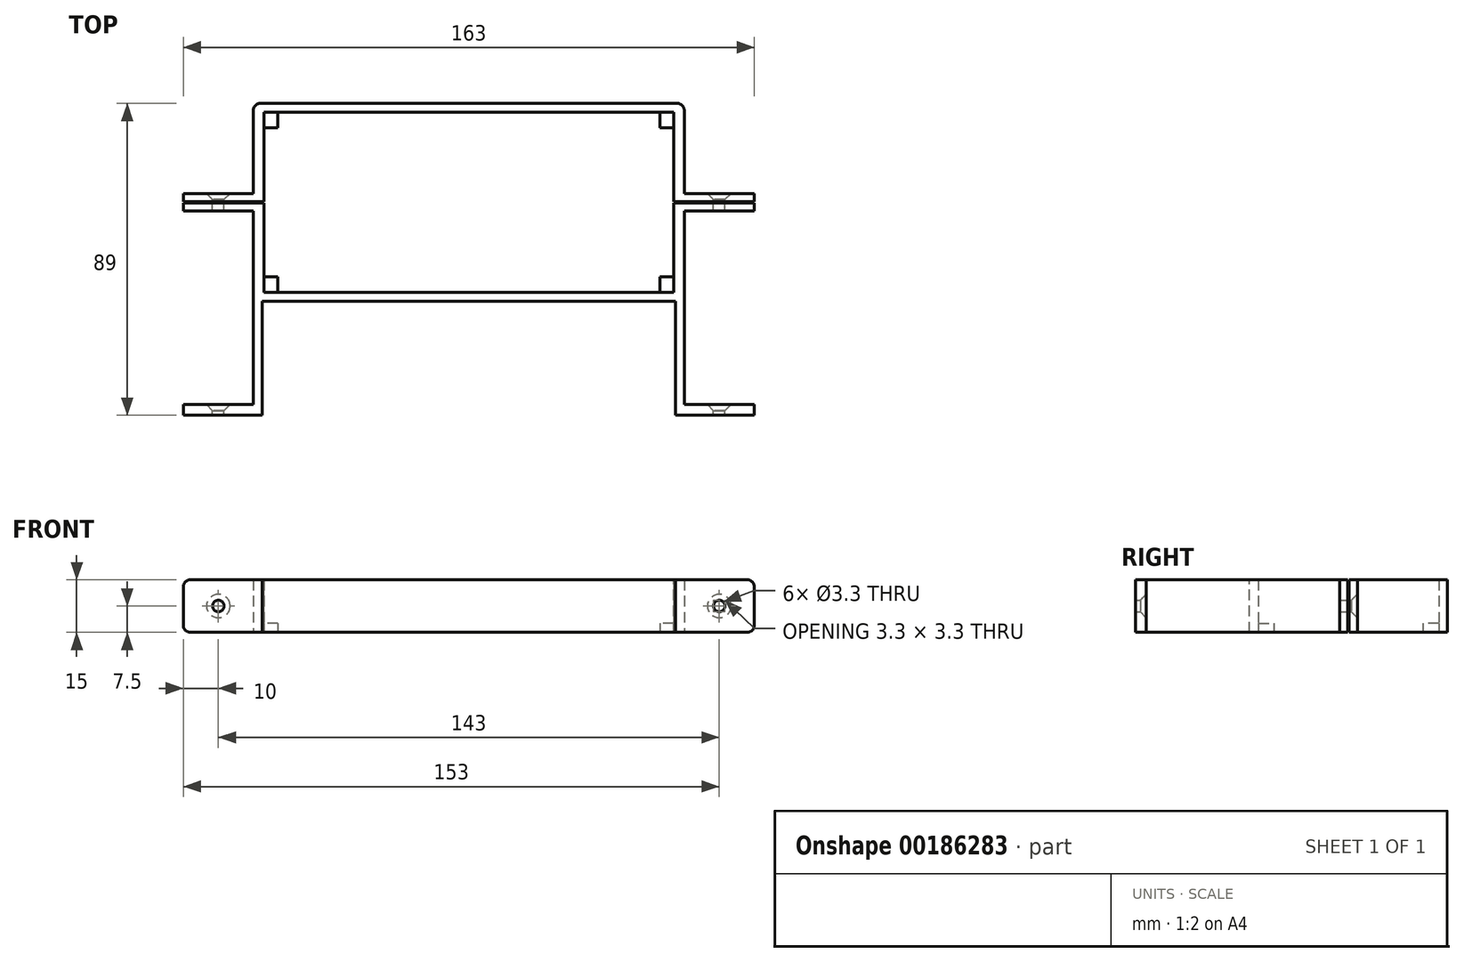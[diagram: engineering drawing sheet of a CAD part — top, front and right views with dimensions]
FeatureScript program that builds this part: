
annotation { "Feature Type Name" : "Feature", "Feature Type Description" : "" }
export const myFeature = defineFeature(function(context is Context, id is Id, definition is map)
    precondition{}
    {
        {
            var Q0;
            Q0=qCreatedBy(makeId("Top.planeOp"),FACE);
            var sketch = newSketch(context, id + "F0", { "sketchPlane" : qUnion([Q0])});
            skLineSegment(sketch, "E0.bottom", {"start": v(61.5, -28.25) * mm, "end": v(-61.5, -28.25) * mm});
            skLineSegment(sketch, "E0.top", {"start": v(61.5, 28.25) * mm, "end": v(-61.5, 28.25) * mm});
            skLineSegment(sketch, "E0.left", {"start": v(61.5, -28.25) * mm, "end": v(61.5, 28.25) * mm});
            skLineSegment(sketch, "E0.right", {"start": v(-61.5, -28.25) * mm, "end": v(-61.5, 28.25) * mm});
            skPoint(sketch, "E0.middle", {"position": v(0, 0) * mm});
            skLineSegment(sketch, "E1.bottom", {"start": v(58.5, -25.75) * mm, "end": v(-58.5, -25.75) * mm});
            skLineSegment(sketch, "E1.top", {"start": v(58.5, 25.75) * mm, "end": v(-58.5, 25.75) * mm});
            skLineSegment(sketch, "E1.left", {"start": v(58.5, -25.75) * mm, "end": v(58.5, 25.75) * mm});
            skLineSegment(sketch, "E1.right", {"start": v(-58.5, -25.75) * mm, "end": v(-58.5, 25.75) * mm});
            skSolve(sketch);
        }
        {
            var Q0;
            Q0=makeQuery(id+"F0.imprint","IMPRINT",FACE,{"disambiguationData":[TD([[makeQuery(id+"F0.imprint","IMPRINT",EDGE,{"derivedFrom":sQuery(id+"F0.wireOp",EDGE,"E0.bottom")}),-1.0]])]});
            extrude(context, id + "F1", {"entities" : qUnion([Q0]), "depth" : 15 * mm, "offsetDistance" : 25 * mm});
        }
        {
            var Q0;
            Q0=makeQuery(id+"F1.opExtrude","CAP_FACE",FACE,{"disambiguationData":[OSD([sQuery(id+"F0.wireOp",EDGE,"E0.bottom"),sQuery(id+"F0.wireOp",EDGE,"E0.top"),sQuery(id+"F0.wireOp",EDGE,"E0.left"),sQuery(id+"F0.wireOp",EDGE,"E0.right"),sQuery(id+"F0.wireOp",EDGE,"E1.bottom"),sQuery(id+"F0.wireOp",EDGE,"E1.top"),sQuery(id+"F0.wireOp",EDGE,"E1.left"),sQuery(id+"F0.wireOp",EDGE,"E1.right")])],"isStart":false});
            var sketch = newSketch(context, id + "F2", { "sketchPlane" : qUnion([Q0])});
            skLineSegment(sketch, "E2.bottom", {"start": v(-55, -25) * mm, "end": v(55, -25) * mm});
            skLineSegment(sketch, "E2.top", {"start": v(-55, 25) * mm, "end": v(55, 25) * mm});
            skLineSegment(sketch, "E2.left", {"start": v(-55, -25) * mm, "end": v(-55, 25) * mm});
            skLineSegment(sketch, "E2.right", {"start": v(55, -25) * mm, "end": v(55, 25) * mm});
            skPoint(sketch, "E2.middle", {"position": v(0, 0) * mm});
            skSolve(sketch);
        }
        {
            var Q0;
            Q0=makeQuery(id+"F1.opExtrude","SWEPT_FACE",FACE,{"disambiguationData":[OSD([sQuery(id+"F0.wireOp",EDGE,"E0.bottom")])]});
            var sketch = newSketch(context, id + "F3", { "sketchPlane" : qUnion([Q0])});
            skPoint(sketch, "E3", {"position": v(-59, 15) * mm});
            skPoint(sketch, "E4", {"position": v(-59, 0) * mm});
            skPoint(sketch, "E5", {"position": v(59, 15) * mm});
            skPoint(sketch, "E6", {"position": v(59, 0) * mm});
            skLineSegment(sketch, "E7", {"start": v(-59, 15) * mm, "end": v(-59, 0) * mm});
            skLineSegment(sketch, "E8", {"start": v(59, 0) * mm, "end": v(59, 15) * mm});
            skSolve(sketch);
        }
        {
            var Q0;
            {var subQ0=sQuery(id+"F3.wireOp",EDGE,"E7");Q0=makeQuery(id+"F3.imprint","IMPRINT",FACE,{"disambiguationData":[TD([[makeQuery(id+"F3.imprint","IMPRINT",EDGE,{"derivedFrom":subQ0}),-1.0]])]});}
            var Q1;
            {var subQ0=sQuery(id+"F3.wireOp",EDGE,"E8");Q1=makeQuery(id+"F3.imprint","IMPRINT",FACE,{"disambiguationData":[TD([[makeQuery(id+"F3.imprint","IMPRINT",EDGE,{"derivedFrom":subQ0}),-1.0]])]});}
            extrude(context, id + "F4", {"entities" : qUnion([Q0, Q1]), "operationType" : NewBodyOperationType.ADD, "depth" : 32.5 * mm, "offsetDistance" : 25 * mm});
        }
        {
            var Q0;
            {var subQ0=sQuery(id+"F0.wireOp",EDGE,"E0.right");Q0=makeQuery(id+"F4.boolean.opBoolean","MERGE",FACE,{"derivedFrom":[makeQuery(id+"F1.opExtrude","SWEPT_FACE",FACE,{"disambiguationData":[OSD([subQ0])]}),makeQuery(id+"F4.opExtrude","SWEPT_FACE",FACE,{"disambiguationData":[OSD([sQuery(id+"F0.wireOp",EDGE,"E0.bottom"),subQ0])]})]});}
            var sketch = newSketch(context, id + "F5", { "sketchPlane" : qUnion([Q0])});
            skPoint(sketch, "E9", {"position": v(57.75, 15) * mm});
            skPoint(sketch, "E10", {"position": v(57.75, 0) * mm});
            skLineSegment(sketch, "E11", {"start": v(57.75, 15) * mm, "end": v(57.75, 0) * mm});
            skSolve(sketch);
        }
        {
            var Q0;
            {var subQ0=sQuery(id+"F5.wireOp",EDGE,"E11");Q0=makeQuery(id+"F5.imprint","IMPRINT",FACE,{"disambiguationData":[TD([[makeQuery(id+"F5.imprint","IMPRINT",EDGE,{"derivedFrom":subQ0}),1.0]])]});}
            extrude(context, id + "F6", {"entities" : qUnion([Q0]), "operationType" : NewBodyOperationType.ADD, "depth" : 20 * mm, "offsetDistance" : 25 * mm});
        }
        {
            var Q0;
            {var subQ0=sQuery(id+"F0.wireOp",EDGE,"E0.left");Q0=makeQuery(id+"F4.boolean.opBoolean","MERGE",FACE,{"derivedFrom":[makeQuery(id+"F1.opExtrude","SWEPT_FACE",FACE,{"disambiguationData":[OSD([subQ0])]}),makeQuery(id+"F4.opExtrude","SWEPT_FACE",FACE,{"disambiguationData":[OSD([sQuery(id+"F0.wireOp",EDGE,"E0.bottom"),subQ0])]})]});}
            var sketch = newSketch(context, id + "F7", { "sketchPlane" : qUnion([Q0])});
            skPoint(sketch, "E12", {"position": v(-57.75, 15) * mm});
            skPoint(sketch, "E13", {"position": v(-57.75, 0) * mm});
            skLineSegment(sketch, "E14", {"start": v(-57.75, 15) * mm, "end": v(-57.75, 0) * mm});
            skSolve(sketch);
        }
        {
            var Q0;
            {var subQ0=sQuery(id+"F7.wireOp",EDGE,"E14");Q0=makeQuery(id+"F7.imprint","IMPRINT",FACE,{"disambiguationData":[TD([[makeQuery(id+"F7.imprint","IMPRINT",EDGE,{"derivedFrom":subQ0}),-1.0]])]});}
            extrude(context, id + "F8", {"entities" : qUnion([Q0]), "operationType" : NewBodyOperationType.ADD, "depth" : 20 * mm, "offsetDistance" : 25 * mm});
        }
        {
            var Q0;
            Q0=makeQuery(id+"F8.opExtrude","SWEPT_FACE",FACE,{"disambiguationData":[OSD([sQuery(id+"F7.wireOp",EDGE,"E14")])]});
            var sketch = newSketch(context, id + "F9", { "sketchPlane" : qUnion([Q0])});
            skPoint(sketch, "E15", {"position": v(-71.5, 7.5) * mm});
            skPoint(sketch, "E15.positionSnap0", {"position": v(-71.5, 0) * mm});
            skPoint(sketch, "E15.positionSnap1", {"position": v(-61.5, 7.5) * mm});
            skSolve(sketch);
        }
        {
            var Q0;
            Q0=sQuery(id+"F9.wireOp",VERTEX,"E15");
            var Q1;
            Q1=makeQuery(id+"F1.opExtrude","SWEPT_BODY",BODY,{"disambiguationData":[OSD([sQuery(id+"F0.wireOp",EDGE,"E0.bottom"),sQuery(id+"F0.wireOp",EDGE,"E0.top"),sQuery(id+"F0.wireOp",EDGE,"E0.left"),sQuery(id+"F0.wireOp",EDGE,"E0.right"),sQuery(id+"F0.wireOp",EDGE,"E1.bottom"),sQuery(id+"F0.wireOp",EDGE,"E1.top"),sQuery(id+"F0.wireOp",EDGE,"E1.left"),sQuery(id+"F0.wireOp",EDGE,"E1.right")])]});
            hole(context, id + "F10", {"style" : HoleStyle.C_SINK, "endStyle" : HoleEndStyle.BLIND, "standardTappedOrClearance" : lookupTablePath({ "standard" : "ISO", "fit" : "Normal", "size" : "M3", "type" : "Clearance" }), "standardBlindInLast" : lookupTablePath({ "fit" : "Standard", "standard" : "ISO", "size" : "M3", "type" : "Clearance" }), "holeDiameter" : 3.3 * mm, "cSinkDiameter" : 6.72 * mm, "cSinkAngle" : 90 * degree, "majorDiameter" : 5 * mm, "holeDepth" : 5 * mm, "isTappedThrough" : true, "tappedDepth" : 12 * mm, "tapClearance" : 3, "startFromSketch" : true, "locations" : qUnion([Q0]), "scope" : qUnion([Q1])});
        }
        {
            var Q0;
            Q0=makeQuery(id+"F6.opExtrude","SWEPT_FACE",FACE,{"disambiguationData":[OSD([sQuery(id+"F5.wireOp",EDGE,"E11")])]});
            var sketch = newSketch(context, id + "F11", { "sketchPlane" : qUnion([Q0])});
            skPoint(sketch, "E16", {"position": v(71.5, 7.5) * mm});
            skPoint(sketch, "E16.positionSnap0", {"position": v(81.5, 7.5) * mm});
            skPoint(sketch, "E16.positionSnap1", {"position": v(71.5, 0) * mm});
            skSolve(sketch);
        }
        {
            var Q0;
            Q0=sQuery(id+"F11.wireOp",VERTEX,"E16");
            var Q1;
            Q1=makeQuery(id+"F1.opExtrude","SWEPT_BODY",BODY,{"disambiguationData":[OSD([sQuery(id+"F0.wireOp",EDGE,"E0.bottom"),sQuery(id+"F0.wireOp",EDGE,"E0.top"),sQuery(id+"F0.wireOp",EDGE,"E0.left"),sQuery(id+"F0.wireOp",EDGE,"E0.right"),sQuery(id+"F0.wireOp",EDGE,"E1.bottom"),sQuery(id+"F0.wireOp",EDGE,"E1.top"),sQuery(id+"F0.wireOp",EDGE,"E1.left"),sQuery(id+"F0.wireOp",EDGE,"E1.right")])]});
            hole(context, id + "F12", {"style" : HoleStyle.C_SINK, "endStyle" : HoleEndStyle.BLIND, "standardTappedOrClearance" : lookupTablePath({ "standard" : "ISO", "fit" : "Normal", "size" : "M3", "type" : "Clearance" }), "standardBlindInLast" : lookupTablePath({ "fit" : "Standard", "standard" : "ISO", "size" : "M3", "type" : "Clearance" }), "holeDiameter" : 3.3 * mm, "cSinkDiameter" : 6.72 * mm, "cSinkAngle" : 90 * degree, "majorDiameter" : 5 * mm, "holeDepth" : 5 * mm, "isTappedThrough" : true, "tappedDepth" : 12 * mm, "tapClearance" : 3, "startFromSketch" : true, "locations" : qUnion([Q0]), "scope" : qUnion([Q1])});
        }
        {
            var Q0;
            {var subQ0=sQuery(id+"F0.wireOp",EDGE,"E0.bottom");var subQ1=makeQuery(id+"F1.opExtrude","CAP_EDGE",EDGE,{"disambiguationData":[OSD([subQ0])],"isStart":true});var subQ2=sQuery(id+"F0.wireOp",EDGE,"E0.left");var subQ3=makeQuery(id+"F3.imprint","INTERSECT",VERTEX,{"derivedFrom":[makeQuery(id+"F1.opExtrude","SWEPT_EDGE",EDGE,{"disambiguationData":[OSD([subQ0,subQ2])]}),subQ1]});var subQ4=makeQuery(id+"F4.boolean.opBoolean","MERGE",EDGE,{"derivedFrom":[makeQuery(id+"F1.opExtrude","CAP_EDGE",EDGE,{"disambiguationData":[OSD([subQ2])],"isStart":true}),makeQuery(id+"F4.opExtrude","SWEPT_EDGE",EDGE,{"disambiguationData":[OSD([subQ0,subQ2]),TDD([subQ3])]})]});var subQ5=sQuery(id+"F0.wireOp",EDGE,"E0.right");var subQ6=makeQuery(id+"F3.imprint","INTERSECT",VERTEX,{"derivedFrom":[makeQuery(id+"F1.opExtrude","SWEPT_EDGE",EDGE,{"disambiguationData":[OSD([subQ0,subQ5])]}),subQ1]});var subQ7=makeQuery(id+"F4.boolean.opBoolean","MERGE",EDGE,{"derivedFrom":[makeQuery(id+"F1.opExtrude","CAP_EDGE",EDGE,{"disambiguationData":[OSD([subQ5])],"isStart":true}),makeQuery(id+"F4.opExtrude","SWEPT_EDGE",EDGE,{"disambiguationData":[OSD([subQ0,subQ5]),TDD([subQ6])]})]});Q0=makeQuery(id+"F8.boolean.opBoolean","MERGE",FACE,{"derivedFrom":[makeQuery(id+"F6.boolean.opBoolean","MERGE",FACE,{"derivedFrom":[makeQuery(id+"F4.boolean.opBoolean","MERGE",FACE,{"derivedFrom":[makeQuery(id+"F1.opExtrude","CAP_FACE",FACE,{"disambiguationData":[OSD([subQ0,sQuery(id+"F0.wireOp",EDGE,"E0.top"),subQ2,subQ5,sQuery(id+"F0.wireOp",EDGE,"E1.bottom"),sQuery(id+"F0.wireOp",EDGE,"E1.top"),sQuery(id+"F0.wireOp",EDGE,"E1.left"),sQuery(id+"F0.wireOp",EDGE,"E1.right")])],"isStart":true}),makeQuery(id+"F4.opExtrude","SWEPT_FACE",FACE,{"disambiguationData":[OSD([subQ0]),TDD([makeQuery(id+"F3.imprint","IMPRINT",EDGE,{"disambiguationData":[TD([[makeQuery(id+"F3.imprint","INTERSECT",VERTEX,{"derivedFrom":[subQ1,sQuery(id+"F3.wireOp",EDGE,"E8")]}),1.0]])],"derivedFrom":subQ1})])]}),makeQuery(id+"F4.opExtrude","SWEPT_FACE",FACE,{"disambiguationData":[OSD([subQ0]),TDD([makeQuery(id+"F3.imprint","IMPRINT",EDGE,{"disambiguationData":[TD([[makeQuery(id+"F3.imprint","INTERSECT",VERTEX,{"derivedFrom":[subQ1,sQuery(id+"F3.wireOp",EDGE,"E7")]}),-1.0]])],"derivedFrom":subQ1})])]})]}),makeQuery(id+"F6.opExtrude","SWEPT_FACE",FACE,{"disambiguationData":[OSD([subQ0,subQ5]),TDD([makeQuery(id+"F5.imprint","IMPRINT",EDGE,{"disambiguationData":[TD([[makeQuery(id+"F5.imprint","INTERSECT",VERTEX,{"derivedFrom":[subQ7,sQuery(id+"F5.wireOp",EDGE,"E11")]}),1.0]])],"derivedFrom":subQ7})])]})]}),makeQuery(id+"F8.opExtrude","SWEPT_FACE",FACE,{"disambiguationData":[OSD([subQ0,subQ2]),TDD([makeQuery(id+"F7.imprint","IMPRINT",EDGE,{"disambiguationData":[TD([[makeQuery(id+"F7.imprint","INTERSECT",VERTEX,{"derivedFrom":[subQ4,sQuery(id+"F7.wireOp",EDGE,"E14")]}),1.0]])],"derivedFrom":subQ4})])]})]});}
            var sketch = newSketch(context, id + "F13", { "sketchPlane" : qUnion([Q0])});
            skPoint(sketch, "E17", {"position": v(59.5, -26.25) * mm});
            skPoint(sketch, "E18", {"position": v(-59.5, -26.25) * mm});
            skPoint(sketch, "E19", {"position": v(-59.5, 26.25) * mm});
            skPoint(sketch, "E20", {"position": v(59.5, 26.25) * mm});
            skLineSegment(sketch, "E21.bottom", {"start": v(59.5, -26.25) * mm, "end": v(54.5, -26.25) * mm});
            skLineSegment(sketch, "E21.top", {"start": v(59.5, -21.25) * mm, "end": v(54.5, -21.25) * mm});
            skLineSegment(sketch, "E21.left", {"start": v(59.5, -26.25) * mm, "end": v(59.5, -21.25) * mm});
            skLineSegment(sketch, "E21.right", {"start": v(54.5, -26.25) * mm, "end": v(54.5, -21.25) * mm});
            skLineSegment(sketch, "E22.bottom", {"start": v(-59.5, -26.25) * mm, "end": v(-54.5, -26.25) * mm});
            skLineSegment(sketch, "E22.top", {"start": v(-59.5, -21.25) * mm, "end": v(-54.5, -21.25) * mm});
            skLineSegment(sketch, "E22.left", {"start": v(-59.5, -26.25) * mm, "end": v(-59.5, -21.25) * mm});
            skLineSegment(sketch, "E22.right", {"start": v(-54.5, -26.25) * mm, "end": v(-54.5, -21.25) * mm});
            skLineSegment(sketch, "E23.bottom", {"start": v(-59.5, 26.25) * mm, "end": v(-54.5, 26.25) * mm});
            skLineSegment(sketch, "E23.top", {"start": v(-59.5, 21.25) * mm, "end": v(-54.5, 21.25) * mm});
            skLineSegment(sketch, "E23.left", {"start": v(-59.5, 26.25) * mm, "end": v(-59.5, 21.25) * mm});
            skLineSegment(sketch, "E23.right", {"start": v(-54.5, 26.25) * mm, "end": v(-54.5, 21.25) * mm});
            skLineSegment(sketch, "E24.bottom", {"start": v(59.5, 26.25) * mm, "end": v(54.5, 26.25) * mm});
            skLineSegment(sketch, "E24.top", {"start": v(59.5, 21.25) * mm, "end": v(54.5, 21.25) * mm});
            skLineSegment(sketch, "E24.left", {"start": v(59.5, 26.25) * mm, "end": v(59.5, 21.25) * mm});
            skLineSegment(sketch, "E24.right", {"start": v(54.5, 26.25) * mm, "end": v(54.5, 21.25) * mm});
            skSolve(sketch);
        }
        {
            var Q0;
            {var subQ0=sQuery(id+"F13.wireOp",EDGE,"E22.right");var subQ1=sQuery(id+"F13.wireOp",EDGE,"E22.top");var subQ2=makeQuery(id+"F13.imprint","INTERSECT",VERTEX,{"derivedFrom":[subQ1,subQ0]});Q0=makeQuery(id+"F13.imprint","IMPRINT",FACE,{"disambiguationData":[TD([[makeQuery(id+"F13.imprint","IMPRINT",EDGE,{"disambiguationData":[TD([[subQ2,1.0]])],"derivedFrom":subQ1}),-1.0]])]});}
            var Q1;
            {var subQ0=sQuery(id+"F13.wireOp",EDGE,"E23.right");var subQ1=sQuery(id+"F13.wireOp",EDGE,"E23.top");var subQ2=makeQuery(id+"F13.imprint","INTERSECT",VERTEX,{"derivedFrom":[subQ1,subQ0]});Q1=makeQuery(id+"F13.imprint","IMPRINT",FACE,{"disambiguationData":[TD([[makeQuery(id+"F13.imprint","IMPRINT",EDGE,{"disambiguationData":[TD([[subQ2,1.0]])],"derivedFrom":subQ1}),1.0]])]});}
            var Q2;
            {var subQ0=sQuery(id+"F13.wireOp",EDGE,"E24.right");var subQ1=sQuery(id+"F13.wireOp",EDGE,"E24.top");var subQ2=makeQuery(id+"F13.imprint","INTERSECT",VERTEX,{"derivedFrom":[subQ1,subQ0]});Q2=makeQuery(id+"F13.imprint","IMPRINT",FACE,{"disambiguationData":[TD([[makeQuery(id+"F13.imprint","IMPRINT",EDGE,{"disambiguationData":[TD([[subQ2,1.0]])],"derivedFrom":subQ1}),-1.0]])]});}
            var Q3;
            {var subQ0=sQuery(id+"F13.wireOp",EDGE,"E21.right");var subQ1=sQuery(id+"F13.wireOp",EDGE,"E21.top");var subQ2=makeQuery(id+"F13.imprint","INTERSECT",VERTEX,{"derivedFrom":[subQ1,subQ0]});Q3=makeQuery(id+"F13.imprint","IMPRINT",FACE,{"disambiguationData":[TD([[makeQuery(id+"F13.imprint","IMPRINT",EDGE,{"disambiguationData":[TD([[subQ2,1.0]])],"derivedFrom":subQ1}),1.0]])]});}
            extrude(context, id + "F14", {"entities" : qUnion([Q0, Q1, Q2, Q3]), "operationType" : NewBodyOperationType.ADD, "oppositeDirection" : true, "depth" : 2.5 * mm, "offsetDistance" : 25 * mm});
        }
        {
            var Q0;
            {var subQ0=sQuery(id+"F0.wireOp",EDGE,"E0.right");Q0=makeQuery(id+"F4.boolean.opBoolean","MERGE",FACE,{"derivedFrom":[makeQuery(id+"F1.opExtrude","SWEPT_FACE",FACE,{"disambiguationData":[OSD([subQ0])]}),makeQuery(id+"F4.opExtrude","SWEPT_FACE",FACE,{"disambiguationData":[OSD([sQuery(id+"F0.wireOp",EDGE,"E0.bottom"),subQ0])]})]});}
            var sketch = newSketch(context, id + "F15", { "sketchPlane" : qUnion([Q0])});
            skPoint(sketch, "E25", {"position": v(-2.5, 0) * mm});
            skPoint(sketch, "E26", {"position": v(2.5, 0) * mm});
            skPoint(sketch, "E27", {"position": v(2.5, 15) * mm});
            skPoint(sketch, "E28", {"position": v(-2.5, 15) * mm});
            skPoint(sketch, "E29", {"position": v(0, 0) * mm});
            skPoint(sketch, "E30", {"position": v(0, 15) * mm});
            skLineSegment(sketch, "E31", {"start": v(-2.5, 0) * mm, "end": v(-2.5, 15) * mm});
            skLineSegment(sketch, "E32", {"start": v(2.5, 15) * mm, "end": v(2.5, 0) * mm});
            skSolve(sketch);
        }
        {
            var Q0;
            {var subQ0=sQuery(id+"F15.wireOp",EDGE,"E31");Q0=makeQuery(id+"F15.imprint","IMPRINT",FACE,{"disambiguationData":[TD([[makeQuery(id+"F15.imprint","IMPRINT",EDGE,{"derivedFrom":subQ0}),-1.0]])]});}
            extrude(context, id + "F16", {"entities" : qUnion([Q0]), "operationType" : NewBodyOperationType.ADD, "depth" : 20 * mm, "offsetDistance" : 25 * mm});
        }
        {
            var Q0;
            Q0=makeQuery(id+"F16.opExtrude","SWEPT_FACE",FACE,{"disambiguationData":[OSD([sQuery(id+"F15.wireOp",EDGE,"E31")])]});
            var sketch = newSketch(context, id + "F17", { "sketchPlane" : qUnion([Q0])});
            skPoint(sketch, "E33", {"position": v(71.5, 7.5) * mm});
            skPoint(sketch, "E33.positionSnap0", {"position": v(71.5, 0) * mm});
            skPoint(sketch, "E33.positionSnap1", {"position": v(81.5, 7.5) * mm});
            skSolve(sketch);
        }
        {
            var Q0;
            Q0=sQuery(id+"F17.wireOp",VERTEX,"E33");
            var Q1;
            Q1=makeQuery(id+"F1.opExtrude","SWEPT_BODY",BODY,{"disambiguationData":[OSD([sQuery(id+"F0.wireOp",EDGE,"E0.bottom"),sQuery(id+"F0.wireOp",EDGE,"E0.top"),sQuery(id+"F0.wireOp",EDGE,"E0.left"),sQuery(id+"F0.wireOp",EDGE,"E0.right"),sQuery(id+"F0.wireOp",EDGE,"E1.bottom"),sQuery(id+"F0.wireOp",EDGE,"E1.top"),sQuery(id+"F0.wireOp",EDGE,"E1.left"),sQuery(id+"F0.wireOp",EDGE,"E1.right")])]});
            hole(context, id + "F18", {"style" : HoleStyle.C_SINK, "endStyle" : HoleEndStyle.THROUGH, "standardTappedOrClearance" : lookupTablePath({ "standard" : "ISO", "fit" : "Normal", "size" : "M3", "type" : "Clearance" }), "standardBlindInLast" : lookupTablePath({ "fit" : "Standard", "standard" : "ISO", "size" : "M3", "type" : "Clearance" }), "holeDiameter" : 3.3 * mm, "cSinkDiameter" : 6.72 * mm, "cSinkAngle" : 90 * degree, "majorDiameter" : 5 * mm, "isTappedThrough" : true, "tappedDepth" : 12 * mm, "tapClearance" : 3, "startFromSketch" : true, "locations" : qUnion([Q0]), "scope" : qUnion([Q1])});
        }
        {
            var Q0;
            {var subQ0=sQuery(id+"F0.wireOp",EDGE,"E0.left");Q0=makeQuery(id+"F4.boolean.opBoolean","MERGE",FACE,{"derivedFrom":[makeQuery(id+"F1.opExtrude","SWEPT_FACE",FACE,{"disambiguationData":[OSD([subQ0])]}),makeQuery(id+"F4.opExtrude","SWEPT_FACE",FACE,{"disambiguationData":[OSD([sQuery(id+"F0.wireOp",EDGE,"E0.bottom"),subQ0])]})]});}
            var sketch = newSketch(context, id + "F19", { "sketchPlane" : qUnion([Q0])});
            skPoint(sketch, "E34", {"position": v(0, 0) * mm});
            skPoint(sketch, "E35", {"position": v(0, 15) * mm});
            skPoint(sketch, "E36", {"position": v(2.5, 15) * mm});
            skPoint(sketch, "E37", {"position": v(2.5, 0) * mm});
            skPoint(sketch, "E38", {"position": v(-2.5, 0) * mm});
            skPoint(sketch, "E39", {"position": v(-2.5, 15) * mm});
            skLineSegment(sketch, "E40", {"start": v(-2.5, 15) * mm, "end": v(-2.5, 0) * mm});
            skLineSegment(sketch, "E41", {"start": v(2.5, 0) * mm, "end": v(2.5, 15) * mm});
            skSolve(sketch);
        }
        {
            var Q0;
            {var subQ0=sQuery(id+"F19.wireOp",EDGE,"E40");Q0=makeQuery(id+"F19.imprint","IMPRINT",FACE,{"disambiguationData":[TD([[makeQuery(id+"F19.imprint","IMPRINT",EDGE,{"derivedFrom":subQ0}),1.0]])]});}
            extrude(context, id + "F20", {"entities" : qUnion([Q0]), "operationType" : NewBodyOperationType.ADD, "depth" : 20 * mm, "offsetDistance" : 25 * mm});
        }
        {
            var Q0;
            Q0=makeQuery(id+"F20.opExtrude","SWEPT_FACE",FACE,{"disambiguationData":[OSD([sQuery(id+"F19.wireOp",EDGE,"E41")])]});
            var sketch = newSketch(context, id + "F21", { "sketchPlane" : qUnion([Q0])});
            skPoint(sketch, "E42", {"position": v(-71.5, 7.5) * mm});
            skPoint(sketch, "E42.positionSnap0", {"position": v(-71.5, 15) * mm});
            skPoint(sketch, "E42.positionSnap1", {"position": v(-81.5, 7.5) * mm});
            skSolve(sketch);
        }
        {
            var Q0;
            Q0=sQuery(id+"F21.wireOp",VERTEX,"E42");
            var Q1;
            Q1=makeQuery(id+"F1.opExtrude","SWEPT_BODY",BODY,{"disambiguationData":[OSD([sQuery(id+"F0.wireOp",EDGE,"E0.bottom"),sQuery(id+"F0.wireOp",EDGE,"E0.top"),sQuery(id+"F0.wireOp",EDGE,"E0.left"),sQuery(id+"F0.wireOp",EDGE,"E0.right"),sQuery(id+"F0.wireOp",EDGE,"E1.bottom"),sQuery(id+"F0.wireOp",EDGE,"E1.top"),sQuery(id+"F0.wireOp",EDGE,"E1.left"),sQuery(id+"F0.wireOp",EDGE,"E1.right")])]});
            hole(context, id + "F22", {"style" : HoleStyle.C_SINK, "endStyle" : HoleEndStyle.THROUGH, "standardTappedOrClearance" : lookupTablePath({ "standard" : "ISO", "fit" : "Normal", "size" : "M3", "type" : "Clearance" }), "standardBlindInLast" : lookupTablePath({ "fit" : "Standard", "standard" : "ISO", "size" : "M3", "type" : "Clearance" }), "holeDiameter" : 3.3 * mm, "cSinkDiameter" : 6.72 * mm, "cSinkAngle" : 90 * degree, "majorDiameter" : 5 * mm, "isTappedThrough" : true, "tappedDepth" : 12 * mm, "tapClearance" : 3, "startFromSketch" : true, "locations" : qUnion([Q0]), "scope" : qUnion([Q1])});
        }
        {
            var Q0;
            Q0=makeQuery(id+"F20.opExtrude","CAP_FACE",FACE,{"disambiguationData":[OSD([sQuery(id+"F0.wireOp",EDGE,"E0.bottom"),sQuery(id+"F0.wireOp",EDGE,"E0.left"),sQuery(id+"F19.wireOp",EDGE,"E40"),sQuery(id+"F19.wireOp",EDGE,"E41")])],"isStart":false});
            var sketch = newSketch(context, id + "F23", { "sketchPlane" : qUnion([Q0])});
            skPoint(sketch, "E43", {"position": v(0, 0) * mm});
            skPoint(sketch, "E44", {"position": v(0, 15) * mm});
            skPoint(sketch, "E45", {"position": v(0.2, 15) * mm});
            skPoint(sketch, "E46", {"position": v(-0.2, 15) * mm});
            skPoint(sketch, "E47", {"position": v(-0.2, 0) * mm});
            skPoint(sketch, "E48", {"position": v(0.2, 0) * mm});
            skLineSegment(sketch, "E49", {"start": v(-0.2, 15) * mm, "end": v(-0.2, 0) * mm});
            skLineSegment(sketch, "E50", {"start": v(0.2, 0) * mm, "end": v(0.2, 15) * mm});
            skSolve(sketch);
        }
        {
            var Q0;
            {var subQ0=sQuery(id+"F23.wireOp",EDGE,"E49");Q0=makeQuery(id+"F23.imprint","IMPRINT",FACE,{"disambiguationData":[TD([[makeQuery(id+"F23.imprint","IMPRINT",EDGE,{"derivedFrom":subQ0}),1.0]])]});}
            extrude(context, id + "F24", {"entities" : qUnion([Q0]), "operationType" : NewBodyOperationType.REMOVE, "oppositeDirection" : true, "depth" : 200 * mm, "offsetDistance" : 25 * mm});
        }
        {
            var Q0;
            Q0=makeQuery(id+"F1.opExtrude","SWEPT_EDGE",EDGE,{"disambiguationData":[OSD([sQuery(id+"F0.wireOp",EDGE,"E0.top"),sQuery(id+"F0.wireOp",EDGE,"E0.right")])]});
            var Q1;
            {var subQ0=sQuery(id+"F0.wireOp",EDGE,"E0.bottom");var subQ1=sQuery(id+"F0.wireOp",EDGE,"E0.right");var subQ2=makeQuery(id+"F4.boolean.opBoolean","MERGE",EDGE,{"derivedFrom":[makeQuery(id+"F1.opExtrude","CAP_EDGE",EDGE,{"disambiguationData":[OSD([subQ1])],"isStart":true}),makeQuery(id+"F4.opExtrude","SWEPT_EDGE",EDGE,{"disambiguationData":[OSD([subQ0,subQ1]),TDD([makeQuery(id+"F3.imprint","INTERSECT",VERTEX,{"derivedFrom":[makeQuery(id+"F1.opExtrude","SWEPT_EDGE",EDGE,{"disambiguationData":[OSD([subQ0,subQ1])]}),makeQuery(id+"F1.opExtrude","CAP_EDGE",EDGE,{"disambiguationData":[OSD([subQ0])],"isStart":true})]})])]})]});Q1=makeQuery(id+"F6.opExtrude","CAP_EDGE",EDGE,{"disambiguationData":[OSD([subQ0,subQ1]),TDD([makeQuery(id+"F5.imprint","IMPRINT",EDGE,{"disambiguationData":[TD([[makeQuery(id+"F5.imprint","INTERSECT",VERTEX,{"derivedFrom":[subQ2,sQuery(id+"F5.wireOp",EDGE,"E11")]}),1.0]])],"derivedFrom":subQ2})])],"isStart":false});}
            var Q2;
            {var subQ0=sQuery(id+"F0.wireOp",EDGE,"E0.bottom");var subQ1=sQuery(id+"F0.wireOp",EDGE,"E0.right");var subQ2=makeQuery(id+"F4.boolean.opBoolean","MERGE",EDGE,{"derivedFrom":[makeQuery(id+"F1.opExtrude","CAP_EDGE",EDGE,{"disambiguationData":[OSD([subQ1])],"isStart":false}),makeQuery(id+"F4.opExtrude","SWEPT_EDGE",EDGE,{"disambiguationData":[OSD([subQ0,subQ1]),TDD([makeQuery(id+"F3.imprint","INTERSECT",VERTEX,{"derivedFrom":[makeQuery(id+"F1.opExtrude","SWEPT_EDGE",EDGE,{"disambiguationData":[OSD([subQ0,subQ1])]}),makeQuery(id+"F1.opExtrude","CAP_EDGE",EDGE,{"disambiguationData":[OSD([subQ0])],"isStart":false})]})])]})]});Q2=makeQuery(id+"F6.opExtrude","CAP_EDGE",EDGE,{"disambiguationData":[OSD([subQ0,subQ1]),TDD([makeQuery(id+"F5.imprint","IMPRINT",EDGE,{"disambiguationData":[TD([[makeQuery(id+"F5.imprint","INTERSECT",VERTEX,{"derivedFrom":[subQ2,sQuery(id+"F5.wireOp",EDGE,"E11")]}),1.0]])],"derivedFrom":subQ2})])],"isStart":false});}
            var Q3;
            {var subQ0=sQuery(id+"F0.wireOp",EDGE,"E0.bottom");var subQ1=sQuery(id+"F0.wireOp",EDGE,"E0.left");var subQ2=makeQuery(id+"F4.boolean.opBoolean","MERGE",EDGE,{"derivedFrom":[makeQuery(id+"F1.opExtrude","CAP_EDGE",EDGE,{"disambiguationData":[OSD([subQ1])],"isStart":true}),makeQuery(id+"F4.opExtrude","SWEPT_EDGE",EDGE,{"disambiguationData":[OSD([subQ0,subQ1]),TDD([makeQuery(id+"F3.imprint","INTERSECT",VERTEX,{"derivedFrom":[makeQuery(id+"F1.opExtrude","SWEPT_EDGE",EDGE,{"disambiguationData":[OSD([subQ0,subQ1])]}),makeQuery(id+"F1.opExtrude","CAP_EDGE",EDGE,{"disambiguationData":[OSD([subQ0])],"isStart":true})]})])]})]});Q3=makeQuery(id+"F8.opExtrude","CAP_EDGE",EDGE,{"disambiguationData":[OSD([subQ0,subQ1]),TDD([makeQuery(id+"F7.imprint","IMPRINT",EDGE,{"disambiguationData":[TD([[makeQuery(id+"F7.imprint","INTERSECT",VERTEX,{"derivedFrom":[subQ2,sQuery(id+"F7.wireOp",EDGE,"E14")]}),1.0]])],"derivedFrom":subQ2})])],"isStart":false});}
            var Q4;
            {var subQ0=sQuery(id+"F0.wireOp",EDGE,"E0.bottom");var subQ1=sQuery(id+"F0.wireOp",EDGE,"E0.left");var subQ2=makeQuery(id+"F4.boolean.opBoolean","MERGE",EDGE,{"derivedFrom":[makeQuery(id+"F1.opExtrude","CAP_EDGE",EDGE,{"disambiguationData":[OSD([subQ1])],"isStart":false}),makeQuery(id+"F4.opExtrude","SWEPT_EDGE",EDGE,{"disambiguationData":[OSD([subQ0,subQ1]),TDD([makeQuery(id+"F3.imprint","INTERSECT",VERTEX,{"derivedFrom":[makeQuery(id+"F1.opExtrude","SWEPT_EDGE",EDGE,{"disambiguationData":[OSD([subQ0,subQ1])]}),makeQuery(id+"F1.opExtrude","CAP_EDGE",EDGE,{"disambiguationData":[OSD([subQ0])],"isStart":false})]})])]})]});Q4=makeQuery(id+"F8.opExtrude","CAP_EDGE",EDGE,{"disambiguationData":[OSD([subQ0,subQ1]),TDD([makeQuery(id+"F7.imprint","IMPRINT",EDGE,{"disambiguationData":[TD([[makeQuery(id+"F7.imprint","INTERSECT",VERTEX,{"derivedFrom":[subQ2,sQuery(id+"F7.wireOp",EDGE,"E14")]}),1.0]])],"derivedFrom":subQ2})])],"isStart":false});}
            var Q5;
            Q5=makeQuery(id+"F1.opExtrude","SWEPT_EDGE",EDGE,{"disambiguationData":[OSD([sQuery(id+"F0.wireOp",EDGE,"E0.top"),sQuery(id+"F0.wireOp",EDGE,"E0.left")])]});
            var Q6;
            Q6=makeQuery(id+"F6.opExtrude","CAP_EDGE",EDGE,{"disambiguationData":[OSD([sQuery(id+"F5.wireOp",EDGE,"E11")])],"isStart":true});
            var Q7;
            Q7=makeQuery(id+"F8.opExtrude","CAP_EDGE",EDGE,{"disambiguationData":[OSD([sQuery(id+"F7.wireOp",EDGE,"E14")])],"isStart":true});
            var Q8;
            {var subQ2=sQuery(id+"F0.wireOp",EDGE,"E0.bottom");var subQ3=makeQuery(id+"F1.opExtrude","CAP_EDGE",EDGE,{"disambiguationData":[OSD([subQ2])],"isStart":true});var subQ10=sQuery(id+"F0.wireOp",EDGE,"E0.left");var subQ11=makeQuery(id+"F3.imprint","INTERSECT",VERTEX,{"derivedFrom":[makeQuery(id+"F1.opExtrude","SWEPT_EDGE",EDGE,{"disambiguationData":[OSD([subQ2,subQ10])]}),subQ3]});var subQ12=makeQuery(id+"F4.boolean.opBoolean","MERGE",EDGE,{"derivedFrom":[makeQuery(id+"F1.opExtrude","CAP_EDGE",EDGE,{"disambiguationData":[OSD([subQ10])],"isStart":true}),makeQuery(id+"F4.opExtrude","SWEPT_EDGE",EDGE,{"disambiguationData":[OSD([subQ2,subQ10]),TDD([subQ11])]})]});var subQ13=sQuery(id+"F19.wireOp",EDGE,"E40");var subQ15=subQ12;var subQ16=makeQuery(id+"F19.imprint","IMPRINT",EDGE,{"disambiguationData":[TD([[makeQuery(id+"F19.imprint","INTERSECT",VERTEX,{"derivedFrom":[subQ15,subQ13]}),-1.0]])],"derivedFrom":subQ15});Q8=makeQuery(id+"F24.boolean.opBoolean","SPLIT",EDGE,{"disambiguationData":[TD([makeQuery(id+"F20.opExtrude","SWEPT_FACE",FACE,{"disambiguationData":[OSD([subQ13])]})])],"derivedFrom":makeQuery(id+"F20.opExtrude","CAP_EDGE",EDGE,{"disambiguationData":[OSD([subQ2,subQ10]),TDD([subQ16])],"isStart":false})});}
            var Q9;
            {var subQ2=sQuery(id+"F0.wireOp",EDGE,"E0.bottom");var subQ3=makeQuery(id+"F1.opExtrude","CAP_EDGE",EDGE,{"disambiguationData":[OSD([subQ2])],"isStart":true});var subQ10=sQuery(id+"F19.wireOp",EDGE,"E41");var subQ11=sQuery(id+"F0.wireOp",EDGE,"E0.left");var subQ12=makeQuery(id+"F3.imprint","INTERSECT",VERTEX,{"derivedFrom":[makeQuery(id+"F1.opExtrude","SWEPT_EDGE",EDGE,{"disambiguationData":[OSD([subQ2,subQ11])]}),subQ3]});var subQ13=makeQuery(id+"F4.boolean.opBoolean","MERGE",EDGE,{"derivedFrom":[makeQuery(id+"F1.opExtrude","CAP_EDGE",EDGE,{"disambiguationData":[OSD([subQ11])],"isStart":true}),makeQuery(id+"F4.opExtrude","SWEPT_EDGE",EDGE,{"disambiguationData":[OSD([subQ2,subQ11]),TDD([subQ12])]})]});var subQ14=sQuery(id+"F19.wireOp",EDGE,"E40");var subQ15=subQ13;var subQ16=makeQuery(id+"F19.imprint","IMPRINT",EDGE,{"disambiguationData":[TD([[makeQuery(id+"F19.imprint","INTERSECT",VERTEX,{"derivedFrom":[subQ15,subQ14]}),-1.0]])],"derivedFrom":subQ15});Q9=makeQuery(id+"F24.boolean.opBoolean","SPLIT",EDGE,{"disambiguationData":[TD([makeQuery(id+"F20.opExtrude","SWEPT_FACE",FACE,{"disambiguationData":[OSD([subQ10])]})])],"derivedFrom":makeQuery(id+"F20.opExtrude","CAP_EDGE",EDGE,{"disambiguationData":[OSD([subQ2,subQ11]),TDD([subQ16])],"isStart":false})});}
            var Q10;
            {var subQ0=sQuery(id+"F0.wireOp",EDGE,"E0.bottom");var subQ1=makeQuery(id+"F1.opExtrude","CAP_EDGE",EDGE,{"disambiguationData":[OSD([subQ0])],"isStart":false});var subQ5=sQuery(id+"F0.wireOp",EDGE,"E0.left");var subQ6=makeQuery(id+"F3.imprint","INTERSECT",VERTEX,{"derivedFrom":[makeQuery(id+"F1.opExtrude","SWEPT_EDGE",EDGE,{"disambiguationData":[OSD([subQ0,subQ5])]}),subQ1]});var subQ7=makeQuery(id+"F4.boolean.opBoolean","MERGE",EDGE,{"derivedFrom":[makeQuery(id+"F1.opExtrude","CAP_EDGE",EDGE,{"disambiguationData":[OSD([subQ5])],"isStart":false}),makeQuery(id+"F4.opExtrude","SWEPT_EDGE",EDGE,{"disambiguationData":[OSD([subQ0,subQ5]),TDD([subQ6])]})]});var subQ9=sQuery(id+"F19.wireOp",EDGE,"E40");var subQ11=subQ7;var subQ12=makeQuery(id+"F19.imprint","IMPRINT",EDGE,{"disambiguationData":[TD([[makeQuery(id+"F19.imprint","INTERSECT",VERTEX,{"derivedFrom":[subQ11,subQ9]}),-1.0]])],"derivedFrom":subQ11});Q10=makeQuery(id+"F24.boolean.opBoolean","SPLIT",EDGE,{"disambiguationData":[TD([makeQuery(id+"F20.opExtrude","SWEPT_FACE",FACE,{"disambiguationData":[OSD([subQ9])]})])],"derivedFrom":makeQuery(id+"F20.opExtrude","CAP_EDGE",EDGE,{"disambiguationData":[OSD([subQ0,subQ5]),TDD([subQ12])],"isStart":false})});}
            var Q11;
            {var subQ0=sQuery(id+"F0.wireOp",EDGE,"E0.bottom");var subQ1=makeQuery(id+"F1.opExtrude","CAP_EDGE",EDGE,{"disambiguationData":[OSD([subQ0])],"isStart":false});var subQ5=sQuery(id+"F0.wireOp",EDGE,"E0.left");var subQ6=makeQuery(id+"F3.imprint","INTERSECT",VERTEX,{"derivedFrom":[makeQuery(id+"F1.opExtrude","SWEPT_EDGE",EDGE,{"disambiguationData":[OSD([subQ0,subQ5])]}),subQ1]});var subQ7=makeQuery(id+"F4.boolean.opBoolean","MERGE",EDGE,{"derivedFrom":[makeQuery(id+"F1.opExtrude","CAP_EDGE",EDGE,{"disambiguationData":[OSD([subQ5])],"isStart":false}),makeQuery(id+"F4.opExtrude","SWEPT_EDGE",EDGE,{"disambiguationData":[OSD([subQ0,subQ5]),TDD([subQ6])]})]});var subQ9=sQuery(id+"F19.wireOp",EDGE,"E41");var subQ10=sQuery(id+"F19.wireOp",EDGE,"E40");var subQ11=subQ7;var subQ12=makeQuery(id+"F19.imprint","IMPRINT",EDGE,{"disambiguationData":[TD([[makeQuery(id+"F19.imprint","INTERSECT",VERTEX,{"derivedFrom":[subQ11,subQ10]}),-1.0]])],"derivedFrom":subQ11});Q11=makeQuery(id+"F24.boolean.opBoolean","SPLIT",EDGE,{"disambiguationData":[TD([makeQuery(id+"F20.opExtrude","SWEPT_FACE",FACE,{"disambiguationData":[OSD([subQ9])]})])],"derivedFrom":makeQuery(id+"F20.opExtrude","CAP_EDGE",EDGE,{"disambiguationData":[OSD([subQ0,subQ5]),TDD([subQ12])],"isStart":false})});}
            var Q12;
            {var subQ0=sQuery(id+"F0.wireOp",EDGE,"E0.bottom");var subQ1=makeQuery(id+"F1.opExtrude","CAP_EDGE",EDGE,{"disambiguationData":[OSD([subQ0])],"isStart":false});var subQ2=sQuery(id+"F0.wireOp",EDGE,"E0.right");var subQ3=makeQuery(id+"F3.imprint","INTERSECT",VERTEX,{"derivedFrom":[makeQuery(id+"F1.opExtrude","SWEPT_EDGE",EDGE,{"disambiguationData":[OSD([subQ0,subQ2])]}),subQ1]});var subQ4=makeQuery(id+"F4.boolean.opBoolean","MERGE",EDGE,{"derivedFrom":[makeQuery(id+"F1.opExtrude","CAP_EDGE",EDGE,{"disambiguationData":[OSD([subQ2])],"isStart":false}),makeQuery(id+"F4.opExtrude","SWEPT_EDGE",EDGE,{"disambiguationData":[OSD([subQ0,subQ2]),TDD([subQ3])]})]});var subQ8=sQuery(id+"F15.wireOp",EDGE,"E31");var subQ9=subQ4;var subQ10=sQuery(id+"F15.wireOp",EDGE,"E32");var subQ11=makeQuery(id+"F15.imprint","IMPRINT",EDGE,{"disambiguationData":[TD([[makeQuery(id+"F15.imprint","INTERSECT",VERTEX,{"derivedFrom":[subQ9,subQ8]}),1.0]])],"derivedFrom":subQ9});Q12=makeQuery(id+"F24.boolean.opBoolean","SPLIT",EDGE,{"disambiguationData":[TD([makeQuery(id+"F16.opExtrude","SWEPT_FACE",FACE,{"disambiguationData":[OSD([subQ10])]})])],"derivedFrom":makeQuery(id+"F16.opExtrude","CAP_EDGE",EDGE,{"disambiguationData":[OSD([subQ0,subQ2]),TDD([subQ11])],"isStart":false})});}
            var Q13;
            {var subQ0=sQuery(id+"F0.wireOp",EDGE,"E0.bottom");var subQ1=makeQuery(id+"F1.opExtrude","CAP_EDGE",EDGE,{"disambiguationData":[OSD([subQ0])],"isStart":false});var subQ2=sQuery(id+"F0.wireOp",EDGE,"E0.right");var subQ3=makeQuery(id+"F3.imprint","INTERSECT",VERTEX,{"derivedFrom":[makeQuery(id+"F1.opExtrude","SWEPT_EDGE",EDGE,{"disambiguationData":[OSD([subQ0,subQ2])]}),subQ1]});var subQ4=makeQuery(id+"F4.boolean.opBoolean","MERGE",EDGE,{"derivedFrom":[makeQuery(id+"F1.opExtrude","CAP_EDGE",EDGE,{"disambiguationData":[OSD([subQ2])],"isStart":false}),makeQuery(id+"F4.opExtrude","SWEPT_EDGE",EDGE,{"disambiguationData":[OSD([subQ0,subQ2]),TDD([subQ3])]})]});var subQ7=sQuery(id+"F15.wireOp",EDGE,"E31");var subQ9=subQ4;var subQ11=makeQuery(id+"F15.imprint","IMPRINT",EDGE,{"disambiguationData":[TD([[makeQuery(id+"F15.imprint","INTERSECT",VERTEX,{"derivedFrom":[subQ9,subQ7]}),1.0]])],"derivedFrom":subQ9});Q13=makeQuery(id+"F24.boolean.opBoolean","SPLIT",EDGE,{"disambiguationData":[TD([makeQuery(id+"F16.opExtrude","SWEPT_FACE",FACE,{"disambiguationData":[OSD([subQ7])]})])],"derivedFrom":makeQuery(id+"F16.opExtrude","CAP_EDGE",EDGE,{"disambiguationData":[OSD([subQ0,subQ2]),TDD([subQ11])],"isStart":false})});}
            var Q14;
            {var subQ2=sQuery(id+"F15.wireOp",EDGE,"E31");var subQ3=sQuery(id+"F0.wireOp",EDGE,"E0.bottom");var subQ4=makeQuery(id+"F1.opExtrude","CAP_EDGE",EDGE,{"disambiguationData":[OSD([subQ3])],"isStart":true});var subQ5=sQuery(id+"F0.wireOp",EDGE,"E0.right");var subQ6=makeQuery(id+"F3.imprint","INTERSECT",VERTEX,{"derivedFrom":[makeQuery(id+"F1.opExtrude","SWEPT_EDGE",EDGE,{"disambiguationData":[OSD([subQ3,subQ5])]}),subQ4]});var subQ7=makeQuery(id+"F4.boolean.opBoolean","MERGE",EDGE,{"derivedFrom":[makeQuery(id+"F1.opExtrude","CAP_EDGE",EDGE,{"disambiguationData":[OSD([subQ5])],"isStart":true}),makeQuery(id+"F4.opExtrude","SWEPT_EDGE",EDGE,{"disambiguationData":[OSD([subQ3,subQ5]),TDD([subQ6])]})]});var subQ14=subQ7;var subQ15=makeQuery(id+"F15.imprint","IMPRINT",EDGE,{"disambiguationData":[TD([[makeQuery(id+"F15.imprint","INTERSECT",VERTEX,{"derivedFrom":[subQ14,subQ2]}),1.0]])],"derivedFrom":subQ14});Q14=makeQuery(id+"F24.boolean.opBoolean","SPLIT",EDGE,{"disambiguationData":[TD([makeQuery(id+"F16.opExtrude","SWEPT_FACE",FACE,{"disambiguationData":[OSD([subQ2])]})])],"derivedFrom":makeQuery(id+"F16.opExtrude","CAP_EDGE",EDGE,{"disambiguationData":[OSD([subQ3,subQ5]),TDD([subQ15])],"isStart":false})});}
            var Q15;
            {var subQ0=sQuery(id+"F15.wireOp",EDGE,"E32");var subQ1=sQuery(id+"F15.wireOp",EDGE,"E31");var subQ2=sQuery(id+"F0.wireOp",EDGE,"E0.right");var subQ3=sQuery(id+"F0.wireOp",EDGE,"E0.bottom");var subQ6=makeQuery(id+"F1.opExtrude","CAP_EDGE",EDGE,{"disambiguationData":[OSD([subQ3])],"isStart":true});var subQ7=makeQuery(id+"F3.imprint","INTERSECT",VERTEX,{"derivedFrom":[makeQuery(id+"F1.opExtrude","SWEPT_EDGE",EDGE,{"disambiguationData":[OSD([subQ3,subQ2])]}),subQ6]});var subQ8=makeQuery(id+"F4.boolean.opBoolean","MERGE",EDGE,{"derivedFrom":[makeQuery(id+"F1.opExtrude","CAP_EDGE",EDGE,{"disambiguationData":[OSD([subQ2])],"isStart":true}),makeQuery(id+"F4.opExtrude","SWEPT_EDGE",EDGE,{"disambiguationData":[OSD([subQ3,subQ2]),TDD([subQ7])]})]});var subQ14=subQ8;var subQ15=makeQuery(id+"F15.imprint","IMPRINT",EDGE,{"disambiguationData":[TD([[makeQuery(id+"F15.imprint","INTERSECT",VERTEX,{"derivedFrom":[subQ14,subQ1]}),1.0]])],"derivedFrom":subQ14});Q15=makeQuery(id+"F24.boolean.opBoolean","SPLIT",EDGE,{"disambiguationData":[TD([makeQuery(id+"F16.opExtrude","SWEPT_FACE",FACE,{"disambiguationData":[OSD([subQ0])]})])],"derivedFrom":makeQuery(id+"F16.opExtrude","CAP_EDGE",EDGE,{"disambiguationData":[OSD([subQ3,subQ2]),TDD([subQ15])],"isStart":false})});}
            var Q16;
            Q16=makeQuery(id+"F16.opExtrude","CAP_EDGE",EDGE,{"disambiguationData":[OSD([sQuery(id+"F15.wireOp",EDGE,"E31")])],"isStart":true});
            var Q17;
            Q17=makeQuery(id+"F16.opExtrude","CAP_EDGE",EDGE,{"disambiguationData":[OSD([sQuery(id+"F15.wireOp",EDGE,"E32")])],"isStart":true});
            var Q18;
            Q18=makeQuery(id+"F20.opExtrude","CAP_EDGE",EDGE,{"disambiguationData":[OSD([sQuery(id+"F19.wireOp",EDGE,"E41")])],"isStart":true});
            var Q19;
            Q19=makeQuery(id+"F20.opExtrude","CAP_EDGE",EDGE,{"disambiguationData":[OSD([sQuery(id+"F19.wireOp",EDGE,"E40")])],"isStart":true});
            fillet(context, id + "F25", {"entities" : qUnion([Q0, Q1, Q2, Q3, Q4, Q5, Q6, Q7, Q8, Q9, Q10, Q11, Q12, Q13, Q14, Q15, Q16, Q17, Q18, Q19]), "radius" : 2 * mm, "tangentPropagation" : true, "allowEdgeOverflow" : false});
        }
    });
